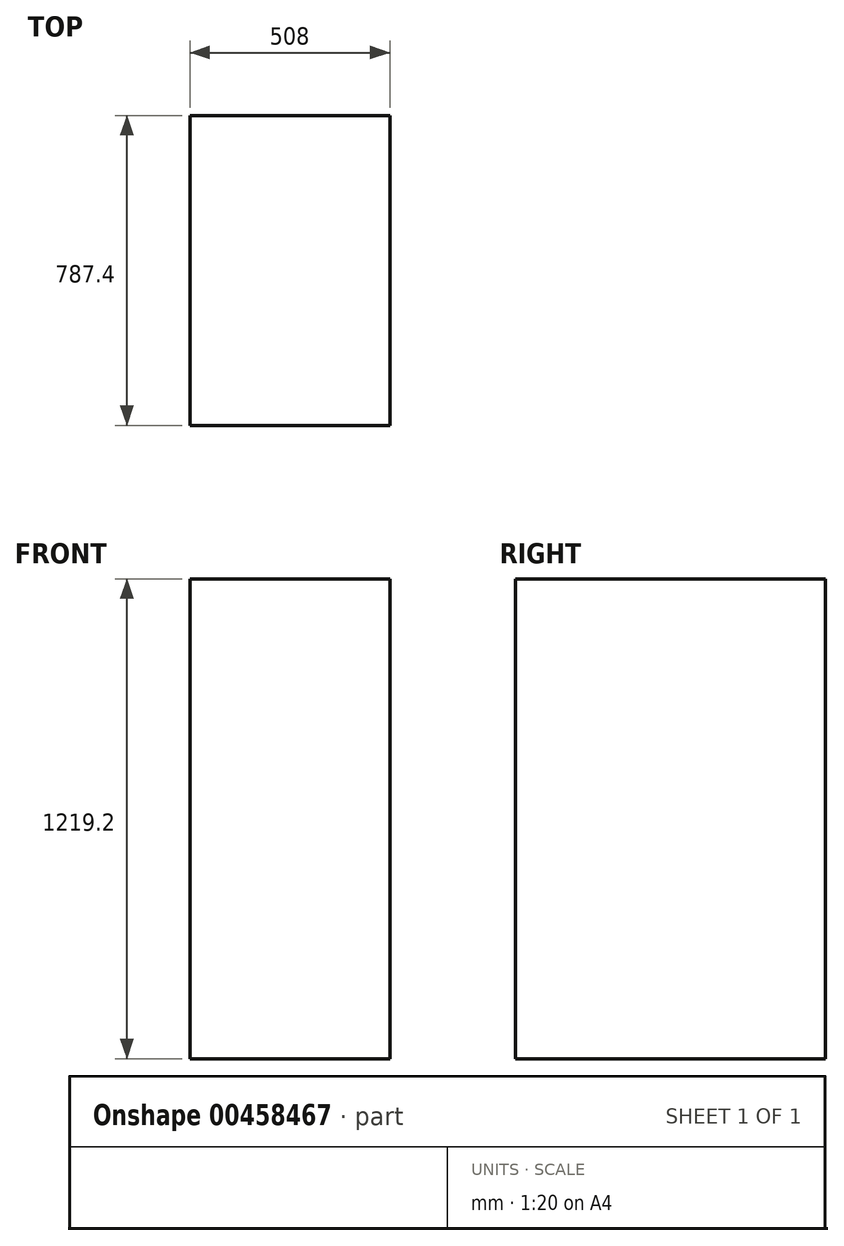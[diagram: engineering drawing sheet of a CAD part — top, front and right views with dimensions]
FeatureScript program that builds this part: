
annotation { "Feature Type Name" : "Feature", "Feature Type Description" : "" }
export const myFeature = defineFeature(function(context is Context, id is Id, definition is map)
    precondition{}
    {
        {
            var Q0;
            Q0=qCreatedBy(makeId("Top.planeOp"),FACE);
            var sketch = newSketch(context, id + "F0", { "sketchPlane" : qUnion([Q0])});
            skLineSegment(sketch, "E0.bottom", {"start": v(-268.17, 660.73) * mm, "end": v(239.83, 660.73) * mm});
            skLineSegment(sketch, "E0.top", {"start": v(-268.17, -126.67) * mm, "end": v(239.83, -126.67) * mm});
            skLineSegment(sketch, "E0.left", {"start": v(-268.17, 660.73) * mm, "end": v(-268.17, -126.67) * mm});
            skLineSegment(sketch, "E0.right", {"start": v(239.83, 660.73) * mm, "end": v(239.83, -126.67) * mm});
            skSolve(sketch);
        }
        {
            var Q0;
            Q0=makeQuery(id+"F0.imprint","IMPRINT",FACE,{"disambiguationData":[TD([[makeQuery(id+"F0.imprint","IMPRINT",EDGE,{"derivedFrom":sQuery(id+"F0.wireOp",EDGE,"E0.bottom")}),-1.0]])]});
            extrude(context, id + "F1", {"entities" : qUnion([Q0]), "depth" : 1219.2 * mm});
        }
    });
